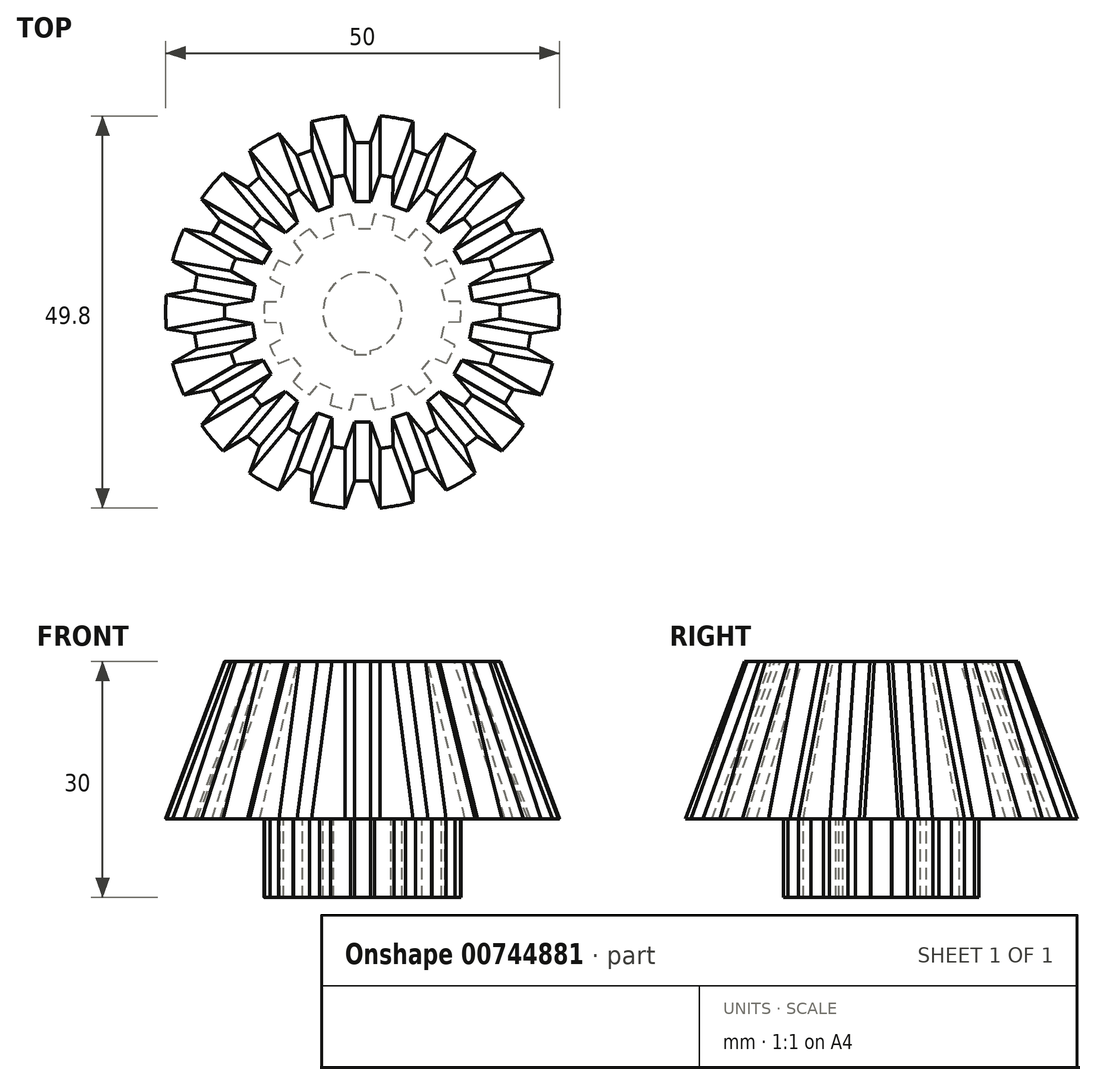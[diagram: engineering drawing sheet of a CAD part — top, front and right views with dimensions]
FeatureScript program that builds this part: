
annotation { "Feature Type Name" : "Feature", "Feature Type Description" : "" }
export const myFeature = defineFeature(function(context is Context, id is Id, definition is map)
    precondition{}
    {
        {
            var Q0;
            Q0=qCreatedBy(makeId("Top.planeOp"),FACE);
            var sketch = newSketch(context, id + "F0", { "sketchPlane" : qUnion([Q0])});
            skCircle(sketch, "E0", {"center": v(0, 0) * mm, "radius": 25 * mm});
            skSolve(sketch);
        }
        {
            var Q0;
            Q0=qCreatedBy(makeId("Top.planeOp"),FACE);
            cPlane(context, id + "F1", {"entities" : qUnion([Q0]), "cplaneType" : CPlaneType.OFFSET, "offset" : 20 * mm, "width" : 150 * mm, "height" : 150 * mm});
        }
        {
            var Q0;
            Q0=qCreatedBy(id+"F1.planeOp",FACE);
            var sketch = newSketch(context, id + "F2", { "sketchPlane" : qUnion([Q0])});
            skCircle(sketch, "E1", {"center": v(0, 0) * mm, "radius": 17.5 * mm});
            skSolve(sketch);
        }
        {
            var Q0;
            Q0=makeQuery(id+"F0.imprint","IMPRINT",FACE,{"disambiguationData":[TD([[makeQuery(id+"F0.imprint","IMPRINT",EDGE,{"derivedFrom":sQuery(id+"F0.wireOp",EDGE,"E0")}),1.0]])]});
            var Q1;
            Q1=makeQuery(id+"F2.imprint","IMPRINT",FACE,{"disambiguationData":[TD([[makeQuery(id+"F2.imprint","IMPRINT",EDGE,{"derivedFrom":sQuery(id+"F2.wireOp",EDGE,"E1")}),1.0]])]});
            loft(context, id + "F3", {"sheetProfilesArray" : [{ "sheetProfileEntities" : qUnion([Q0]) }, { "sheetProfileEntities" : qUnion([Q1]) }]});
        }
        {
            var Q0;
            Q0=makeQuery(id+"F3.opLoft","CAP_FACE",FACE,{"disambiguationData":[OSD([makeQuery(id+"F0.imprint","IMPRINT",FACE,{"disambiguationData":[TD([[makeQuery(id+"F0.imprint","IMPRINT",EDGE,{"derivedFrom":sQuery(id+"F0.wireOp",EDGE,"E0")}),1.0]])]})])],"isStart":true});
            var sketch = newSketch(context, id + "F4", { "sketchPlane" : qUnion([Q0])});
            skCircle(sketch, "E2.0.0", {"center": v(0, 0) * mm, "radius": 25 * mm});
            skLineSegment(sketch, "E3", {"start": v(-1, 21.5) * mm, "end": v(1, 21.5) * mm});
            skLineSegment(sketch, "E4", {"start": v(1, 21.5) * mm, "end": v(2.2, 24.9) * mm});
            skLineSegment(sketch, "E5.MirrorCS", {"start": v(-1, 21.5) * mm, "end": v(-2.2, 24.9) * mm});
            skSolve(sketch);
        }
        {
            var Q0;
            Q0=makeQuery(id+"F3.opLoft","CAP_FACE",FACE,{"disambiguationData":[OSD([makeQuery(id+"F2.imprint","IMPRINT",FACE,{"disambiguationData":[TD([[makeQuery(id+"F2.imprint","IMPRINT",EDGE,{"derivedFrom":sQuery(id+"F2.wireOp",EDGE,"E1")}),1.0]])]})])],"isStart":true});
            var sketch = newSketch(context, id + "F5", { "sketchPlane" : qUnion([Q0])});
            skLineSegment(sketch, "E6", {"start": v(-1, -14) * mm, "end": v(1, -14) * mm});
            skLineSegment(sketch, "E7", {"start": v(-1, -14) * mm, "end": v(-2.2, -17.36) * mm});
            skLineSegment(sketch, "E8.MirrorCS", {"start": v(1, -14) * mm, "end": v(2.2, -17.36) * mm});
            skCircle(sketch, "E9.0.0", {"center": v(0, 0) * mm, "radius": 17.5 * mm});
            skSolve(sketch);
        }
        {
            var Q1;
            Q1=makeQuery(id+"F4.imprint","IMPRINT",FACE,{"disambiguationData":[TD([[makeQuery(id+"F4.imprint","IMPRINT",EDGE,{"derivedFrom":sQuery(id+"F4.wireOp",EDGE,"E3")}),1.0]])]});
            var Q2;
            Q2=makeQuery(id+"F5.imprint","IMPRINT",FACE,{"disambiguationData":[TD([[makeQuery(id+"F5.imprint","IMPRINT",EDGE,{"derivedFrom":sQuery(id+"F5.wireOp",EDGE,"E6")}),-1.0]])]});
            loft(context, id + "F6", {"sheetProfilesArray" : [{ "sheetProfileEntities" : qUnion([Q1]) }, { "sheetProfileEntities" : qUnion([Q2]) }]});
        }
        {
            var Q0;
            Q0=makeQuery(id+"F6.opLoft","SWEPT_BODY",BODY,{"disambiguationData":[OSD([makeQuery(id+"F4.imprint","IMPRINT",FACE,{"disambiguationData":[TD([[makeQuery(id+"F4.imprint","IMPRINT",EDGE,{"derivedFrom":sQuery(id+"F4.wireOp",EDGE,"E3")}),1.0]])]}),makeQuery(id+"F5.imprint","IMPRINT",FACE,{"disambiguationData":[TD([[makeQuery(id+"F5.imprint","IMPRINT",EDGE,{"derivedFrom":sQuery(id+"F5.wireOp",EDGE,"E6")}),-1.0]])]})])]});
            var Q1;
            Q1=makeQuery(id+"F3.opLoft","MID_CAP_EDGE",EDGE,{"disambiguationData":[OSD([sQuery(id+"F0.wireOp",EDGE,"E0")])],"capPos":0.0});
            circularPattern(context, id + "F7", {"operationType" : NewBodyOperationType.REMOVE, "entities" : qUnion([Q0]), "axis" : qUnion([Q1]), "angle" : 360 * degree, "instanceCount" : 18, "equalSpace" : true});
        }
        {
            var Q0;
            Q0=makeQuery(id+"F3.opLoft","CAP_FACE",FACE,{"disambiguationData":[OSD([makeQuery(id+"F0.imprint","IMPRINT",FACE,{"disambiguationData":[TD([[makeQuery(id+"F0.imprint","IMPRINT",EDGE,{"derivedFrom":sQuery(id+"F0.wireOp",EDGE,"E0")}),1.0]])]})])],"isStart":true});
            var sketch = newSketch(context, id + "F8", { "sketchPlane" : qUnion([Q0])});
            skCircle(sketch, "E10", {"center": v(0, 0) * mm, "radius": 12.5 * mm});
            skArc(sketch, "E11", {"start": v(-1, 4.9) * mm, "mid": v(0, -5) * mm, "end": v(1, 4.9) * mm});
            skLineSegment(sketch, "E12", {"start": v(-1, 4.9) * mm, "end": v(-1, 5.4) * mm});
            skLineSegment(sketch, "E13", {"start": v(-1, 5.4) * mm, "end": v(1, 5.4) * mm});
            skLineSegment(sketch, "E14", {"start": v(1, 5.4) * mm, "end": v(1, 4.9) * mm});
            skLineSegment(sketch, "E15", {"start": v(-1, 10.5) * mm, "end": v(1, 10.5) * mm});
            skLineSegment(sketch, "E16", {"start": v(1.5, 12.4) * mm, "end": v(1, 10.5) * mm});
            skLineSegment(sketch, "E17.MirrorCS", {"start": v(-1.5, 12.4) * mm, "end": v(-1, 10.5) * mm});
            skSolve(sketch);
        }
        {
            var Q0;
            Q0 = qSketchRegion(id + "F8", true);
            extrude(context, id + "F9", {"entities" : qUnion([Q0]), "operationType" : NewBodyOperationType.ADD, "depth" : 10 * mm, "offsetDistance" : 25 * mm});
        }
        {
            var Q0;
            Q0=makeQuery(id+"F8.imprint","IMPRINT",FACE,{"disambiguationData":[TD([[makeQuery(id+"F8.imprint","IMPRINT",EDGE,{"derivedFrom":sQuery(id+"F8.wireOp",EDGE,"E15")}),1.0]])]});
            extrude(context, id + "F10", {"entities" : qUnion([Q0]), "depth" : 10 * mm, "offsetDistance" : 25 * mm});
        }
        {
            var Q0;
            Q0=makeQuery(id+"F10.opExtrude","SWEPT_BODY",BODY,{"disambiguationData":[OSD([sQuery(id+"F8.wireOp",EDGE,"E10"),sQuery(id+"F8.wireOp",EDGE,"E15"),sQuery(id+"F8.wireOp",EDGE,"E16"),sQuery(id+"F8.wireOp",EDGE,"E17.MirrorCS")])]});
            var Q1;
            Q1=makeQuery(id+"F9.opExtrude","CAP_EDGE",EDGE,{"disambiguationData":[OSD([sQuery(id+"F8.wireOp",EDGE,"E10")])],"isStart":false});
            circularPattern(context, id + "F11", {"operationType" : NewBodyOperationType.REMOVE, "entities" : qUnion([Q0]), "axis" : qUnion([Q1]), "angle" : 360 * degree, "instanceCount" : 14, "equalSpace" : true});
        }
    });
